# Revit family: Plumbing-Valves-Sloan-CX-158
name_source: partatom
category: Plumbing Fixtures
units: mm (PartAtom-declared; Revit-internal decimal feet)

## family parameters
Cut with Voids When Loaded = No
Host = Face
OmniClass Number = 23.45.05.14.99
OmniClass Title = Other Sanitary Washing Plumbing Fixtures
Part Type = Normal
Room Calculation Point = No
Round Connector Dimension = Use Diameter
Shared = No

## types (10) — shared parameters
ADA Compliant = Yes
Assembly Code = D2020300
CW Connection = Yes
Default Elevation = 0"
Edition number = 1
Fixture Inlet to Wall Opening = 6 1/4"
HW Connection = No
Height = 8 1/2"
Keynote = 15410
Manufacturer = Sloan Valve
Operating Water Pressure = 20 – 80 PSI (138 – 552 kPa)
Product Guid = 705ad915-f848-4d48-a022-665c87b04fb2
Product data url = https://bimobject.com
URL = www.sloanvalve.com
Valve CL to Fixture Inlet = 12 1/4"
Valve Pressure Drop = 0.00 psi
Vent Connection = No
Waste Connection = No
Water Inlet Connection Diameter = 2"
Water Outlet Connection Diameter = 2"
Width = 7 1/2"
zero-valued in all types: CWFU, HWFU, WFU

## per-type parameters (varying)
| type | Description | Flush Rate | Part Number | Product Material |
| CX 158-1.28 | 1.28 gpf, Filtered, Polished Chrome Finish, Fixture Connection Rear Spud, Single Flush, Integrated Control Stop, 3.25-4.25 L Dimension, Adjustable Flush Connection Outlet Tube, ADA Compliant Push Button, Short V500A & Adjustable Flush Connection Vacuum Breaker, Front Accessible Wall Box, CX Concealed Manual Water Closet Flushometer. | 1.28 gpf (4.8 Lpf) | 3400201 | Sloan Valve - Finish - Polished Chrome |
| CX 158-1.6 | 1.6 gpf, Filtered, Polished Chrome Finish, Fixture Connection Rear Spud, Single Flush, Integrated Control Stop, 3.25-4.25 L Dimension, Adjustable Flush Connection Outlet Tube, ADA Compliant Push Button, Short V500A & Adjustable Flush Connection Vacuum Breaker, Front Accessible Wall Box, CX Concealed Manual Water Closet Flushometer. | 1.6 gpf (6.0 Lpf) | 3400200 | Sloan Valve - Finish - Polished Chrome |
| CX 158-1.28-BN | 1.28 gpf, Filtered, Brushed Nickel Finish, Fixture Connection Rear Spud, Single Flush, Integrated Control Stop, 3.25-4.25 L Dimension, Adjustable Flush Connection Outlet Tube, ADA Compliant Push Button, Short V500A & Adjustable Flush Connection Vacuum Breaker, Front Accessible Wall Box, CX Concealed Manual Water Closet Flushometer. | 1.28 gpf (4.8 Lpf) | 3400209 | Sloan Valve - Finish - Brushed Nickel |
| CX 158-1.28-GR | 1.28 gpf, Filtered, Graphite Finish, Fixture Connection Rear Spud, Single Flush, Integrated Control Stop, 3.25-4.25 L Dimension, Adjustable Flush Connection Outlet Tube, ADA Compliant Push Button, Short V500A & Adjustable Flush Connection Vacuum Breaker, Front Accessible Wall Box, CX Concealed Manual Water Closet Flushometer. | 1.28 gpf (4.8 Lpf) | 3400217 | Sloan Valve - Finish - Graphite |
| CX 158-1.28-PB | 1.28 gpf, Filtered, Polished Brass Finish, Fixture Connection Rear Spud, Single Flush, Integrated Control Stop, 3.25-4.25 L Dimension, Adjustable Flush Connection Outlet Tube, ADA Compliant Push Button, Short V500A & Adjustable Flush Connection Vacuum Breaker, Front Accessible Wall Box, CX Concealed Manual Water Closet Flushometer. | 1.28 gpf (4.8 Lpf) | 3400213 | Sloan Valve - Finish - Polished Brass |
| CX 158-1.28-SF | 1.28 gpf, Filtered, Brushed Stainless Finish, Fixture Connection Rear Spud, Single Flush, Integrated Control Stop, 3.25-4.25 L Dimension, Adjustable Flush Connection Outlet Tube, ADA Compliant Push Button, Short V500A & Adjustable Flush Connection Vacuum Breaker, CX Concealed Manual Water Closet Flushometer. | 1.28 gpf (4.8 Lpf) | 3400205 | Sloan Valve - Finish - Stainless Steel |
| CX 158-1.6-BN | 1.6 gpf, Filtered, Brushed Nickel Finish, Fixture Connection Rear Spud, Single Flush, Integrated Control Stop, 3.25-4.25 L Dimension, Adjustable Flush Connection Outlet Tube, ADA Compliant Push Button, Short V500A & Adjustable Flush Connection Vacuum Breaker, Front Accessible Wall Box, CX Concealed Manual Water Closet Flushometer. | 1.6 gpf (6.0 Lpf) | 3400208 | Sloan Valve - Finish - Brushed Nickel |
| CX 158-1.6-GR | 1.6 gpf, Filtered, Graphite Finish, Fixture Connection Rear Spud, Single Flush, Integrated Control Stop, 3.25-4.25 L Dimension, Adjustable Flush Connection Outlet Tube, ADA Compliant Push Button, Short V500A & Adjustable Flush Connection Vacuum Breaker, Front Accessible Wall Box, CX Concealed Manual Water Closet Flushometer. | 1.6 gpf (6.0 Lpf) | 3400216 | Sloan Valve - Finish - Graphite |
| CX 158-1.6-PB | 1.6 gpf, Filtered, Polished Brass Finish, Fixture Connection Rear Spud, Single Flush, Integrated Control Stop, 3.25-4.25 L Dimension, Adjustable Flush Connection Outlet Tube, ADA Compliant Push Button, Short V500A & Adjustable Flush Connection Vacuum Breaker, Front Accessible Wall Box, CX Concealed Manual Water Closet Flushometer. | 1.6 gpf (6.0 Lpf) | 3400212 | Sloan Valve - Finish - Polished Brass |
| CX 158-1.6-SF | 1.6 gpf, Filtered, Brushed Stainless Finish, Fixture Connection Rear Spud, Single Flush, Integrated Control Stop, 3.25-4.25 L Dimension, Adjustable Flush Connection Outlet Tube, ADA Compliant Push Button, Short V500A & Adjustable Flush Connection Vacuum Breaker, Front Accessible Wall Box, CX Concealed Manual Water Closet Flushometer. | 1.6 gpf (6.0 Lpf) | 3400204 | Sloan Valve - Finish - Polished Brass |

note: column(s) folded — value = type name in every type: Model

## geometry (parser evidence)
native form markers: Sweep x6
no freeform markers — native parametric forms only
